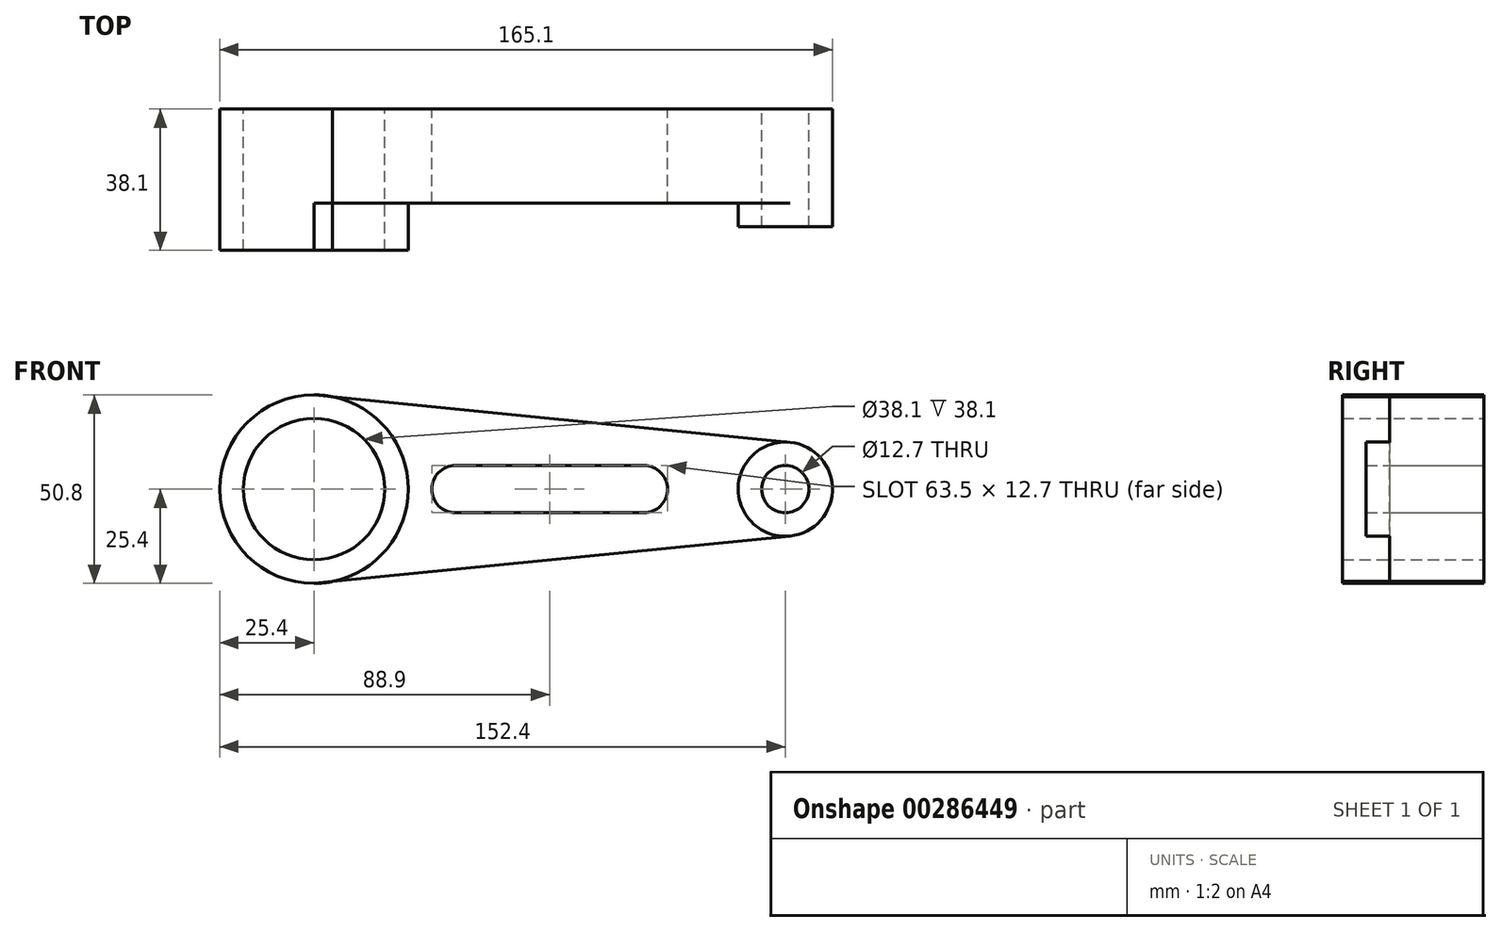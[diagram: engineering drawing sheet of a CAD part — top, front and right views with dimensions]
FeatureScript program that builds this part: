
annotation { "Feature Type Name" : "Feature", "Feature Type Description" : "" }
export const myFeature = defineFeature(function(context is Context, id is Id, definition is map)
    precondition{}
    {
        {
            var Q0;
            Q0=qCreatedBy(makeId("Front.planeOp"),FACE);
            var sketch = newSketch(context, id + "F0", { "sketchPlane" : qUnion([Q0])});
            skCircle(sketch, "E0", {"center": v(0, 0) * mm, "radius": 19.05 * mm});
            skCircle(sketch, "E1", {"center": v(127, 0) * mm, "radius": 6.35 * mm});
            skPoint(sketch, "E2", {"position": v(88.9, 0) * mm});
            skArc(sketch, "E3", {"start": v(38.1, 6.35) * mm, "mid": v(31.75, 0) * mm, "end": v(38.1, -6.35) * mm});
            skCircle(sketch, "E4", {"center": v(127, 0) * mm, "radius": 12.7 * mm});
            skCircle(sketch, "E5", {"center": v(0, 0) * mm, "radius": 25.4 * mm});
            skArc(sketch, "E6", {"start": v(88.9, -6.35) * mm, "mid": v(95.25, 0) * mm, "end": v(88.9, 6.35) * mm});
            skLineSegment(sketch, "E7", {"start": v(38.1, 6.35) * mm, "end": v(88.9, 6.35) * mm});
            skLineSegment(sketch, "E8", {"start": v(38.1, -6.35) * mm, "end": v(88.9, -6.35) * mm});
            skLineSegment(sketch, "E9", {"start": v(0, -25.4) * mm, "end": v(128.26, -12.64) * mm});
            skLineSegment(sketch, "E10", {"start": v(0, 25.4) * mm, "end": v(128.26, 12.64) * mm});
            skSolve(sketch);
        }
        {
            var Q0;
            Q0=makeQuery(id+"F0.imprint","IMPRINT",FACE,{"disambiguationData":[TD([[makeQuery(id+"F0.imprint","IMPRINT",EDGE,{"derivedFrom":sQuery(id+"F0.wireOp",EDGE,"E0")}),-1.0]])]});
            extrude(context, id + "F1", {"entities" : qUnion([Q0]), "depth" : 38.1 * mm});
        }
        {
            var Q0;
            Q0=makeQuery(id+"F0.imprint","IMPRINT",FACE,{"disambiguationData":[TD([[makeQuery(id+"F0.imprint","IMPRINT",EDGE,{"derivedFrom":sQuery(id+"F0.wireOp",EDGE,"E0")}),-1.0]])]});
            var Q1;
            Q1=makeQuery(id+"F0.imprint","IMPRINT",FACE,{"disambiguationData":[TD([[makeQuery(id+"F0.imprint","IMPRINT",EDGE,{"derivedFrom":sQuery(id+"F0.wireOp",EDGE,"E1")}),-1.0]])]});
            extrude(context, id + "F2", {"entities" : qUnion([Q0, Q1]), "operationType" : NewBodyOperationType.ADD, "depth" : 31.75 * mm});
        }
        {
            var Q0;
            Q0 = qSketchRegion(id + "F0", true);
            extrude(context, id + "F3", {"entities" : qUnion([Q0]), "operationType" : NewBodyOperationType.ADD, "depth" : 25.4 * mm});
        }
    });
